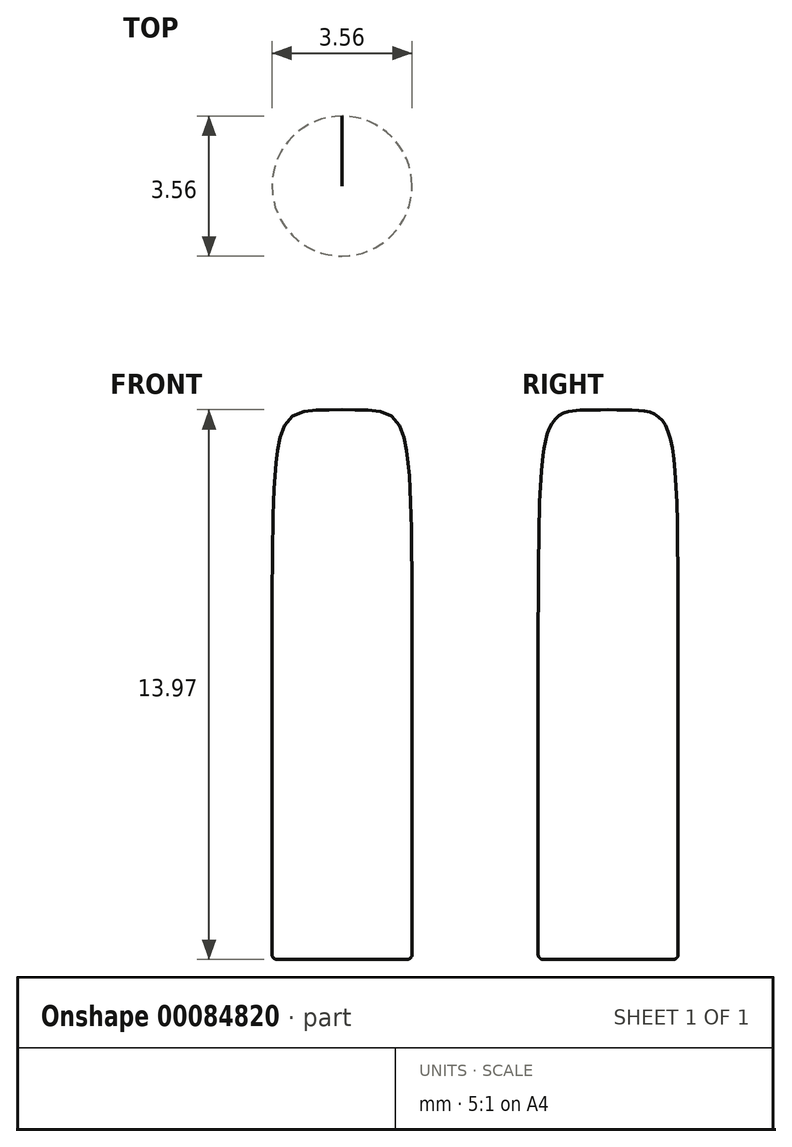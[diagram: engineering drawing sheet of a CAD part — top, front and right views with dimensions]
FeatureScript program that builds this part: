
annotation { "Feature Type Name" : "Feature", "Feature Type Description" : "" }
export const myFeature = defineFeature(function(context is Context, id is Id, definition is map)
    precondition{}
    {
        {
            var Q0;
            Q0=qCreatedBy(makeId("Right.planeOp"),FACE);
            var sketch = newSketch(context, id + "F0", { "sketchPlane" : qUnion([Q0])});
            skLineSegment(sketch, "E0", {"start": v(0, 0) * mm, "end": v(0, 13.97) * mm});
            skLineSegment(sketch, "E1", {"start": v(1.78, 7.62) * mm, "end": v(1.78, 0.13) * mm});
            skLineSegment(sketch, "E2", {"start": v(1.65, 0) * mm, "end": v(0, 0) * mm});
            skFitSpline(sketch, "E3", {"points": [v(0, 13.97) * mm, v(1.78, 7.62) * mm], "startDerivative": vector(5.34, -0.14) * mm, "endDerivative": vector(0.03, -20.4) * mm});
            skPoint(sketch, "E4.visualSharp", {"position": v(1.78, 0) * mm});
            skArc(sketch, "E4.filletArc", {"start": v(1.65, 0) * mm, "mid": v(1.74, 0.04) * mm, "end": v(1.78, 0.13) * mm});
            skSolve(sketch);
        }
        {
            var Q0;
            Q0=qCreatedBy(makeId("Top.planeOp"),FACE);
            var sketch = newSketch(context, id + "F1", { "sketchPlane" : qUnion([Q0])});
            skLineSegment(sketch, "E5.0", {"start": v(0, 1.65) * mm, "end": v(0, 0) * mm});
            skCircle(sketch, "E6", {"center": v(0, 0) * mm, "radius": 1.65 * mm});
            skSolve(sketch);
        }
        {
            var Q0;
            Q0=makeQuery(id+"F0.imprint","IMPRINT",FACE,{"disambiguationData":[TD([[makeQuery(id+"F0.imprint","IMPRINT",EDGE,{"derivedFrom":sQuery(id+"F0.wireOp",EDGE,"E0")}),-1.0]])]});
            var Q1;
            Q1=sQuery(id+"F1.wireOp",EDGE,"E6");
            revolve(context, id + "F2", {"entities" : qUnion([Q0]), "axis" : qUnion([Q1]), "revolveType" : RevolveType.FULL});
        }
    });
